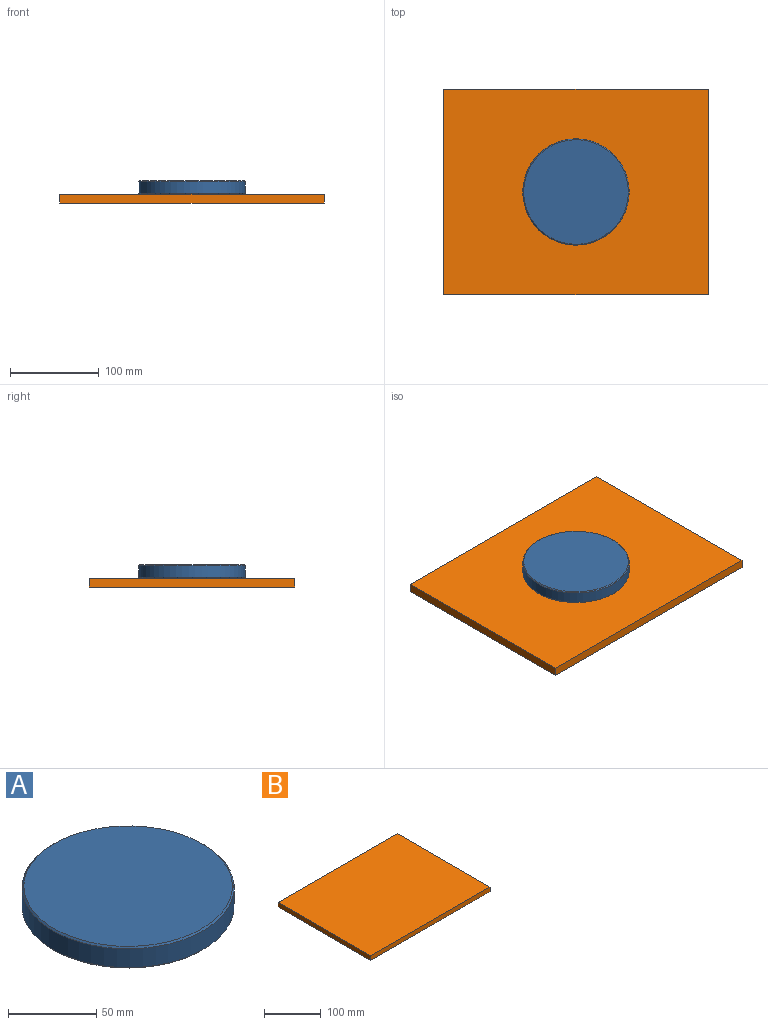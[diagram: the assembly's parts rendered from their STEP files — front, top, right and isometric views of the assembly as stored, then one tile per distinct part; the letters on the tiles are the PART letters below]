
ASSEMBLY  parts=2 mates=1
PART A: 5 faces, bbox 120x120x15 mm
  f0: cylinder r=60mm len=120mm, axis (0,0,-1), area 4900.9mm2, adj f3,f4
  f1: plane 118x118mm, normal (0,0,1), area 10935.9mm2, adj f4
  f2: plane 118x118mm, normal (0,0,-1), area 10935.9mm2, adj f3
  f3: cone r=60mm half-angle=45deg, axis (0,0,1), area 528.7mm2, adj f0,f2
  f4: cone r=59mm half-angle=45deg, axis (0,0,-1), area 528.7mm2, adj f0,f1
PART B: 6 faces, bbox 298.2x231.8x10 mm
  f0: plane 231.83x10mm, normal (-1,0,0), area 2318.3mm2, adj f1,f3,f4,f5
  f1: plane 298.16x10mm, normal (0,-1,0), area 2981.6mm2, adj f0,f2,f4,f5
  f2: plane 231.83x10mm, normal (1,0,0), area 2318.3mm2, adj f1,f3,f4,f5
  f3: plane 298.16x10mm, normal (0,1,0), area 2981.6mm2, adj f0,f2,f4,f5
  f4: plane 298.16x231.83mm, normal (0,0,-1), area 69124.8mm2, adj f0,f1,f2,f3
  f5: plane 298.16x231.83mm, normal (0,0,1), area 69124.8mm2, adj f0,f1,f2,f3
PLACE A t=(-30.28,4.51,77.61)mm
PLACE B t=(-26.62,33.12,77.61)mm
MATE parallel A.f0 <-> B.f5  axis (0,0,-1) through (-30.28,4.51,77.61)mm
